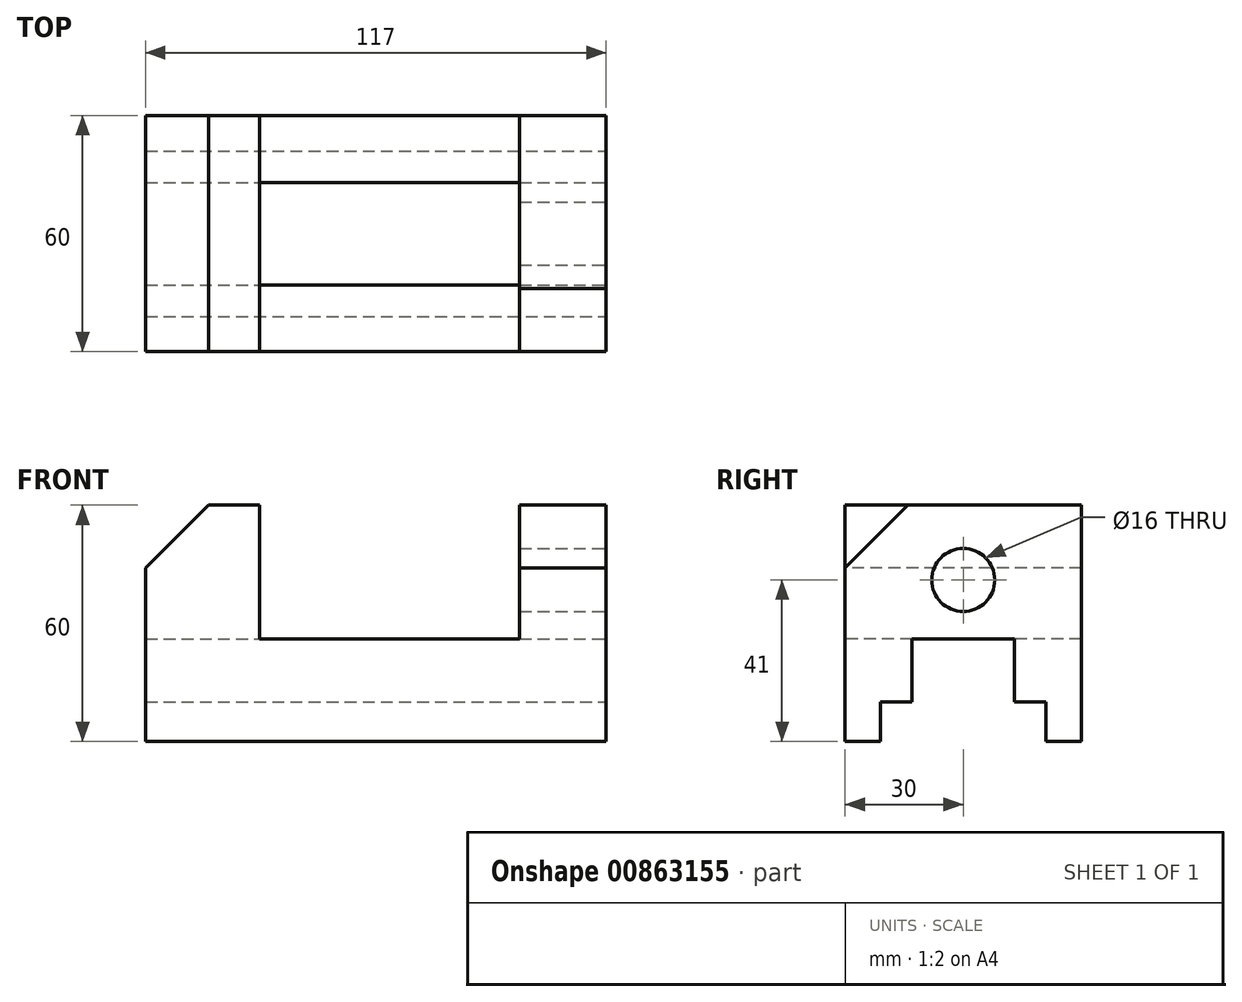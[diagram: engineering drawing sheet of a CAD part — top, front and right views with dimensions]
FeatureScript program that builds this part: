
annotation { "Feature Type Name" : "Feature", "Feature Type Description" : "" }
export const myFeature = defineFeature(function(context is Context, id is Id, definition is map)
    precondition{}
    {
        {
            var Q0;
            Q0=qCreatedBy(makeId("Front.planeOp"),FACE);
            var sketch = newSketch(context, id + "F0", { "sketchPlane" : qUnion([Q0])});
            skLineSegment(sketch, "E0.bottom", {"start": v(58.5, 30) * mm, "end": v(-58.5, 30) * mm});
            skLineSegment(sketch, "E0.top", {"start": v(58.5, -30) * mm, "end": v(-58.5, -30) * mm});
            skLineSegment(sketch, "E0.left", {"start": v(58.5, 30) * mm, "end": v(58.5, -30) * mm});
            skLineSegment(sketch, "E0.right", {"start": v(-58.5, 30) * mm, "end": v(-58.5, -30) * mm});
            skPoint(sketch, "E0.middle", {"position": v(0, 0) * mm});
            skSolve(sketch);
        }
        {
            var Q0;
            Q0=makeQuery(id+"F0.imprint","IMPRINT",FACE,{"disambiguationData":[TD([[makeQuery(id+"F0.imprint","IMPRINT",EDGE,{"derivedFrom":sQuery(id+"F0.wireOp",EDGE,"E0.bottom")}),1.0]])]});
            extrude(context, id + "F1", {"entities" : qUnion([Q0]), "depth" : 60 * mm, "offsetDistance" : 25 * mm});
        }
        {
            var Q0;
            Q0=makeQuery(id+"F1.opExtrude","CAP_FACE",FACE,{"disambiguationData":[OSD([sQuery(id+"F0.wireOp",EDGE,"E0.bottom"),sQuery(id+"F0.wireOp",EDGE,"E0.top"),sQuery(id+"F0.wireOp",EDGE,"E0.left"),sQuery(id+"F0.wireOp",EDGE,"E0.right")])],"isStart":false});
            var sketch = newSketch(context, id + "F2", { "sketchPlane" : qUnion([Q0])});
            skLineSegment(sketch, "E1.bottom", {"start": v(-29.5, 30) * mm, "end": v(36.5, 30) * mm});
            skLineSegment(sketch, "E1.top", {"start": v(-29.5, -4) * mm, "end": v(36.5, -4) * mm});
            skLineSegment(sketch, "E1.left", {"start": v(-29.5, 30) * mm, "end": v(-29.5, -4) * mm});
            skLineSegment(sketch, "E1.right", {"start": v(36.5, 30) * mm, "end": v(36.5, -4) * mm});
            skSolve(sketch);
        }
        {
            var Q0;
            Q0=makeQuery(id+"F2.imprint","IMPRINT",FACE,{"disambiguationData":[TD([[makeQuery(id+"F2.imprint","IMPRINT",EDGE,{"derivedFrom":sQuery(id+"F2.wireOp",EDGE,"E1.bottom")}),1.0]])]});
            extrude(context, id + "F3", {"entities" : qUnion([Q0]), "operationType" : NewBodyOperationType.REMOVE, "endBound" : BoundingType.UP_TO_NEXT, "oppositeDirection" : true, "depth" : 25 * mm, "offsetDistance" : 25 * mm});
        }
        {
            var Q0;
            Q0=makeQuery(id+"F1.opExtrude","CAP_FACE",FACE,{"disambiguationData":[OSD([sQuery(id+"F0.wireOp",EDGE,"E0.bottom"),sQuery(id+"F0.wireOp",EDGE,"E0.top"),sQuery(id+"F0.wireOp",EDGE,"E0.left"),sQuery(id+"F0.wireOp",EDGE,"E0.right")])],"isStart":false});
            var sketch = newSketch(context, id + "F4", { "sketchPlane" : qUnion([Q0])});
            skLineSegment(sketch, "E2", {"start": v(-58.5, 14) * mm, "end": v(-42.5, 30) * mm});
            skLineSegment(sketch, "E3", {"start": v(-42.5, 30) * mm, "end": v(-58.5, 30) * mm});
            skLineSegment(sketch, "E4", {"start": v(-58.5, 30) * mm, "end": v(-58.5, 14) * mm});
            skSolve(sketch);
        }
        {
            var Q0;
            Q0=makeQuery(id+"F4.imprint","IMPRINT",FACE,{"disambiguationData":[TD([[makeQuery(id+"F4.imprint","IMPRINT",EDGE,{"derivedFrom":sQuery(id+"F4.wireOp",EDGE,"E2")}),1.0]])]});
            extrude(context, id + "F5", {"entities" : qUnion([Q0]), "operationType" : NewBodyOperationType.REMOVE, "endBound" : BoundingType.UP_TO_NEXT, "oppositeDirection" : true, "depth" : 25 * mm, "offsetDistance" : 25 * mm});
        }
        {
            var Q0;
            Q0=makeQuery(id+"F1.opExtrude","SWEPT_FACE",FACE,{"disambiguationData":[OSD([sQuery(id+"F0.wireOp",EDGE,"E0.left")])]});
            var sketch = newSketch(context, id + "F6", { "sketchPlane" : qUnion([Q0])});
            skLineSegment(sketch, "E5", {"start": v(-60, 14) * mm, "end": v(-44, 30) * mm});
            skLineSegment(sketch, "E6", {"start": v(-44, 30) * mm, "end": v(-60, 30) * mm});
            skLineSegment(sketch, "E7", {"start": v(-60, 30) * mm, "end": v(-60, 14) * mm});
            skSolve(sketch);
        }
        {
            var Q0;
            Q0=makeQuery(id+"F6.imprint","IMPRINT",FACE,{"disambiguationData":[TD([[makeQuery(id+"F6.imprint","IMPRINT",EDGE,{"derivedFrom":sQuery(id+"F6.wireOp",EDGE,"E5")}),1.0]])]});
            extrude(context, id + "F7", {"entities" : qUnion([Q0]), "operationType" : NewBodyOperationType.REMOVE, "endBound" : BoundingType.UP_TO_NEXT, "oppositeDirection" : true, "depth" : 25 * mm, "offsetDistance" : 25 * mm});
        }
        {
            var Q0;
            Q0=makeQuery(id+"F1.opExtrude","CAP_FACE",FACE,{"disambiguationData":[OSD([sQuery(id+"F0.wireOp",EDGE,"E0.bottom"),sQuery(id+"F0.wireOp",EDGE,"E0.top"),sQuery(id+"F0.wireOp",EDGE,"E0.left"),sQuery(id+"F0.wireOp",EDGE,"E0.right")])],"isStart":false});
            var Q1;
            Q1=makeQuery(id+"F1.opExtrude","CAP_FACE",FACE,{"disambiguationData":[OSD([sQuery(id+"F0.wireOp",EDGE,"E0.bottom"),sQuery(id+"F0.wireOp",EDGE,"E0.top"),sQuery(id+"F0.wireOp",EDGE,"E0.left"),sQuery(id+"F0.wireOp",EDGE,"E0.right")])],"isStart":true});
            cPlane(context, id + "F8", {"entities" : qUnion([Q0, Q1]), "cplaneType" : CPlaneType.MID_PLANE, "offset" : 25 * mm, "width" : 150 * mm, "height" : 150 * mm});
        }
        {
            var Q0;
            Q0=makeQuery(id+"F1.opExtrude","SWEPT_FACE",FACE,{"disambiguationData":[OSD([sQuery(id+"F0.wireOp",EDGE,"E0.left")])]});
            var sketch = newSketch(context, id + "F9", { "sketchPlane" : qUnion([Q0])});
            skLineSegment(sketch, "E8", {"start": v(-51, -30) * mm, "end": v(-51, -20) * mm});
            skLineSegment(sketch, "E9", {"start": v(-51, -20) * mm, "end": v(-43, -20) * mm});
            skLineSegment(sketch, "E10", {"start": v(-43, -20) * mm, "end": v(-43, -4) * mm});
            skLineSegment(sketch, "E11", {"start": v(-43, -4) * mm, "end": v(-17, -4) * mm});
            skLineSegment(sketch, "E12", {"start": v(-17, -4) * mm, "end": v(-17, -20) * mm});
            skLineSegment(sketch, "E13", {"start": v(-17, -20) * mm, "end": v(-9, -20) * mm});
            skLineSegment(sketch, "E14", {"start": v(-9, -20) * mm, "end": v(-9, -30) * mm});
            skLineSegment(sketch, "E15", {"start": v(-9, -30) * mm, "end": v(-51, -30) * mm});
            skPoint(sketch, "E16.startSnap0", {"position": v(-30, -4) * mm});
            skPoint(sketch, "E16.endSnap0", {"position": v(-30, -30) * mm});
            skLineSegment(sketch, "E17.0", {"start": v(-60, -30) * mm, "end": v(0, -30) * mm});
            skSolve(sketch);
        }
        {
            var Q0;
            {var subQ0=sQuery(id+"F9.wireOp",EDGE,"E8");Q0=makeQuery(id+"F9.imprint","IMPRINT",FACE,{"disambiguationData":[TD([[makeQuery(id+"F9.imprint","IMPRINT",EDGE,{"derivedFrom":subQ0}),-1.0]])]});}
            extrude(context, id + "F10", {"entities" : qUnion([Q0]), "operationType" : NewBodyOperationType.REMOVE, "endBound" : BoundingType.THROUGH_ALL, "oppositeDirection" : true, "depth" : 25 * mm, "offsetDistance" : 25 * mm});
        }
        {
            var Q0;
            Q0=makeQuery(id+"F1.opExtrude","SWEPT_FACE",FACE,{"disambiguationData":[OSD([sQuery(id+"F0.wireOp",EDGE,"E0.left")])]});
            var sketch = newSketch(context, id + "F11", { "sketchPlane" : qUnion([Q0])});
            skCircle(sketch, "E18", {"center": v(-30, 11) * mm, "radius": 8 * mm});
            skSolve(sketch);
        }
        {
            var Q0;
            Q0=makeQuery(id+"F11.imprint","IMPRINT",FACE,{"disambiguationData":[TD([[makeQuery(id+"F11.imprint","IMPRINT",EDGE,{"derivedFrom":sQuery(id+"F11.wireOp",EDGE,"E18")}),1.0]])]});
            extrude(context, id + "F12", {"entities" : qUnion([Q0]), "operationType" : NewBodyOperationType.REMOVE, "endBound" : BoundingType.UP_TO_NEXT, "oppositeDirection" : true, "depth" : 25 * mm, "offsetDistance" : 25 * mm});
        }
    });
